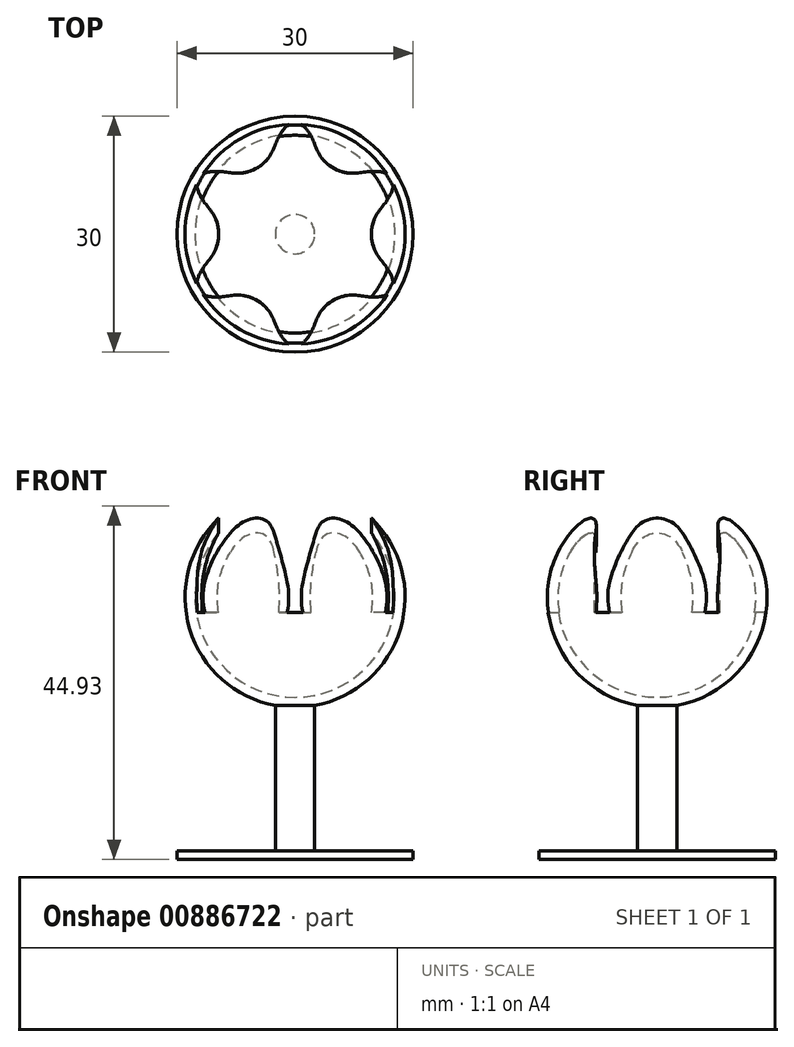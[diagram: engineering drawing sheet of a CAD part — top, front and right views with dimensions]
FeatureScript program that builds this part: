
annotation { "Feature Type Name" : "Feature", "Feature Type Description" : "" }
export const myFeature = defineFeature(function(context is Context, id is Id, definition is map)
    precondition{}
    {
        {
            var Q0;
            Q0=qCreatedBy(makeId("Top.planeOp"),FACE);
            var sketch = newSketch(context, id + "F0", { "sketchPlane" : qUnion([Q0])});
            skCircle(sketch, "E0", {"center": v(0, 0) * mm, "radius": 15 * mm});
            skSolve(sketch);
        }
        {
            var Q0;
            Q0 = qSketchRegion(id + "F0", true);
            extrude(context, id + "F1", {"entities" : qUnion([Q0]), "depth" : 1.1 * mm, "offsetDistance" : 25 * mm});
        }
        {
            var Q0;
            Q0=makeQuery(id+"F1.opExtrude","CAP_FACE",FACE,{"disambiguationData":[OSD([sQuery(id+"F0.wireOp",EDGE,"E0")])],"isStart":false});
            var sketch = newSketch(context, id + "F2", { "sketchPlane" : qUnion([Q0])});
            skCircle(sketch, "E1", {"center": v(0, 0) * mm, "radius": 2.5 * mm});
            skSolve(sketch);
        }
        {
            var Q0;
            Q0 = qSketchRegion(id + "F2", true);
            extrude(context, id + "F3", {"entities" : qUnion([Q0]), "operationType" : NewBodyOperationType.ADD, "depth" : 32.2 * mm, "offsetDistance" : 25 * mm});
        }
        {
            var Q0;
            Q0=makeQuery(id+"F3.opExtrude","CAP_FACE",FACE,{"disambiguationData":[OSD([sQuery(id+"F2.wireOp",EDGE,"E1")])],"isStart":false});
            var sketch = newSketch(context, id + "F4", { "sketchPlane" : qUnion([Q0])});
            skCircle(sketch, "E2", {"center": v(0, 0) * mm, "radius": 13.97 * mm});
            skPoint(sketch, "E3.orphan", {"position": v(0, 12.7) * mm});
            skLineSegment(sketch, "E4", {"start": v(0, 13.97) * mm, "end": v(0, -13.97) * mm});
            skSolve(sketch);
        }
        {
            var Q0;
            {var subQ0=sQuery(id+"F4.wireOp",EDGE,"E4");var subQ1=makeQuery(id+"F3.opExtrude","CAP_EDGE",EDGE,{"disambiguationData":[OSD([sQuery(id+"F2.wireOp",EDGE,"E1")])],"isStart":false});var subQ2=makeQuery(id+"F4.imprint","INTERSECT",VERTEX,{"disambiguationData":[OD(0.0)],"derivedFrom":[subQ1,subQ0]});Q0=makeQuery(id+"F4.imprint","IMPRINT",FACE,{"disambiguationData":[TD([[makeQuery(id+"F4.imprint","IMPRINT",EDGE,{"disambiguationData":[TD([[subQ2,-1.0]])],"derivedFrom":subQ0}),1.0]])]});}
            var sketch = newSketch(context, id + "F5", { "sketchPlane" : qUnion([Q0])});
            skCircle(sketch, "E5", {"center": v(0, 0) * mm, "radius": 12.7 * mm});
            skLineSegment(sketch, "E6", {"start": v(0, 12.7) * mm, "end": v(0, -12.7) * mm});
            skSolve(sketch);
        }
        {
            var Q0;
            {var subQ0=sQuery(id+"F4.wireOp",EDGE,"E4");var subQ1=sQuery(id+"F4.wireOp",EDGE,"E2");var subQ2=makeQuery(id+"F4.imprint","INTERSECT",VERTEX,{"disambiguationData":[OD(0.0)],"derivedFrom":[subQ1,subQ0]});Q0=makeQuery(id+"F4.imprint","IMPRINT",FACE,{"disambiguationData":[TD([[makeQuery(id+"F4.imprint","IMPRINT",EDGE,{"disambiguationData":[TD([[subQ2,-1.0]])],"derivedFrom":subQ1}),1.0]])]});}
            var Q1;
            Q1=sQuery(id+"F4.wireOp",EDGE,"E4");
            revolve(context, id + "F6", {"operationType" : NewBodyOperationType.ADD, "surfaceOperationType" : NewSurfaceOperationType.NEW, "entities" : qUnion([Q0]), "axis" : qUnion([Q1]), "revolveType" : RevolveType.FULL});
        }
        {
            var Q0;
            Q0=makeQuery(id+"F1.opExtrude","CAP_FACE",FACE,{"disambiguationData":[OSD([sQuery(id+"F0.wireOp",EDGE,"E0")])],"isStart":true});
            cPlane(context, id + "F7", {"entities" : qUnion([Q0]), "cplaneType" : CPlaneType.OFFSET, "offset" : 48.4 * mm, "oppositeDirection" : true, "width" : 150 * mm, "height" : 150 * mm});
        }
        {
            var Q0;
            Q0=qCreatedBy(id+"F7.planeOp",FACE);
            var sketch = newSketch(context, id + "F8", { "sketchPlane" : qUnion([Q0])});
            skCircle(sketch, "E7", {"center": v(0, 0) * mm, "radius": 14.16 * mm});
            skSolve(sketch);
        }
        {
            var Q0;
            Q0 = qSketchRegion(id + "F8", true);
            extrude(context, id + "F9", {"entities" : qUnion([Q0]), "operationType" : NewBodyOperationType.REMOVE, "depth" : 4.1 * mm, "offsetDistance" : 25 * mm});
        }
        {
            var Q0;
            Q0=makeQuery(id+"F9.boolean.opBoolean","COPY",FACE,{"derivedFrom":makeQuery(id+"F9.opExtrude","CAP_FACE",FACE,{"disambiguationData":[OSD([sQuery(id+"F8.wireOp",EDGE,"E7")])],"isStart":false})});
            var sketch = newSketch(context, id + "F10", { "sketchPlane" : qUnion([Q0])});
            skEllipse(sketch, "E8", {"center": v(0, 0) * mm, "majorRadius": 14.21 * mm, "minorRadius": 4.2 * mm, "majorAxis": v(0, -1)});
            skEllipse(sketch, "E9.1.0", {"center": v(0, 0) * mm, "majorRadius": 14.21 * mm, "minorRadius": 4.2 * mm, "majorAxis": v(0.87, 0.5)});
            skEllipse(sketch, "E9.2.0", {"center": v(0, 0) * mm, "majorRadius": 14.21 * mm, "minorRadius": 4.2 * mm, "majorAxis": v(-0.87, 0.5)});
            skSolve(sketch);
        }
        {
            var Q0;
            {var subQ0=sQuery(id+"F10.wireOp",EDGE,"E9.2.0");var subQ1=sQuery(id+"F10.wireOp",EDGE,"E8");var subQ2=makeQuery(id+"F10.imprint","INTERSECT",VERTEX,{"disambiguationData":[OD(0.0)],"derivedFrom":[subQ1,subQ0]});Q0=makeQuery(id+"F10.imprint","IMPRINT",FACE,{"disambiguationData":[TD([[makeQuery(id+"F10.imprint","IMPRINT",EDGE,{"disambiguationData":[TD([[subQ2,-1.0]])],"derivedFrom":subQ1}),1.0]])]});}
            var Q1;
            {var subQ0=sQuery(id+"F10.wireOp",EDGE,"E9.1.0");var subQ1=sQuery(id+"F10.wireOp",EDGE,"E8");var subQ2=makeQuery(id+"F10.imprint","INTERSECT",VERTEX,{"disambiguationData":[OD(0.0)],"derivedFrom":[subQ1,subQ0]});Q1=makeQuery(id+"F10.imprint","IMPRINT",FACE,{"disambiguationData":[TD([[makeQuery(id+"F10.imprint","IMPRINT",EDGE,{"disambiguationData":[TD([[subQ2,-1.0]])],"derivedFrom":subQ1}),-1.0]])]});}
            var Q2;
            {var subQ0=sQuery(id+"F10.wireOp",EDGE,"E9.1.0");var subQ1=sQuery(id+"F10.wireOp",EDGE,"E8");var subQ2=makeQuery(id+"F10.imprint","INTERSECT",VERTEX,{"disambiguationData":[OD(0.0)],"derivedFrom":[subQ1,subQ0]});Q2=makeQuery(id+"F10.imprint","IMPRINT",FACE,{"disambiguationData":[TD([[makeQuery(id+"F10.imprint","IMPRINT",EDGE,{"disambiguationData":[TD([[subQ2,-1.0]])],"derivedFrom":subQ1}),1.0]])]});}
            var Q3;
            {var subQ0=sQuery(id+"F10.wireOp",EDGE,"E9.2.0");var subQ1=sQuery(id+"F10.wireOp",EDGE,"E8");var subQ2=makeQuery(id+"F10.imprint","INTERSECT",VERTEX,{"disambiguationData":[OD(2.0)],"derivedFrom":[subQ1,subQ0]});Q3=makeQuery(id+"F10.imprint","IMPRINT",FACE,{"disambiguationData":[TD([[makeQuery(id+"F10.imprint","IMPRINT",EDGE,{"disambiguationData":[TD([[subQ2,-1.0]])],"derivedFrom":subQ1}),1.0]])]});}
            var Q4;
            {var subQ0=sQuery(id+"F10.wireOp",EDGE,"E9.2.0");var subQ1=sQuery(id+"F10.wireOp",EDGE,"E8");var subQ2=makeQuery(id+"F10.imprint","INTERSECT",VERTEX,{"disambiguationData":[OD(3.0)],"derivedFrom":[subQ1,subQ0]});Q4=makeQuery(id+"F10.imprint","IMPRINT",FACE,{"disambiguationData":[TD([[makeQuery(id+"F10.imprint","IMPRINT",EDGE,{"disambiguationData":[TD([[subQ2,-1.0]])],"derivedFrom":subQ1}),1.0]])]});}
            var Q5;
            {var subQ0=sQuery(id+"F10.wireOp",EDGE,"E9.2.0");var subQ1=sQuery(id+"F10.wireOp",EDGE,"E8");var subQ2=makeQuery(id+"F10.imprint","INTERSECT",VERTEX,{"disambiguationData":[OD(3.0)],"derivedFrom":[subQ1,subQ0]});Q5=makeQuery(id+"F10.imprint","IMPRINT",FACE,{"disambiguationData":[TD([[makeQuery(id+"F10.imprint","IMPRINT",EDGE,{"disambiguationData":[TD([[subQ2,-1.0]])],"derivedFrom":subQ1}),-1.0]])]});}
            var Q6;
            {var subQ0=sQuery(id+"F10.wireOp",EDGE,"E9.1.0");var subQ1=makeQuery(id+"F9.boolean.opBoolean","INTERSECT",EDGE,{"derivedFrom":[makeQuery(id+"F6.opRevolve","SWEPT_FACE",FACE,{"disambiguationData":[OSD([sQuery(id+"F4.wireOp",EDGE,"E2")])]}),makeQuery(id+"F9.opExtrude","CAP_FACE",FACE,{"disambiguationData":[OSD([sQuery(id+"F8.wireOp",EDGE,"E7")])],"isStart":false})]});var subQ2=makeQuery(id+"F10.imprint","INTERSECT",VERTEX,{"disambiguationData":[OD(1.0)],"derivedFrom":[subQ1,subQ0]});Q6=makeQuery(id+"F10.imprint","IMPRINT",FACE,{"disambiguationData":[TD([[makeQuery(id+"F10.imprint","IMPRINT",EDGE,{"disambiguationData":[TD([[subQ2,-1.0]])],"derivedFrom":subQ0}),1.0]])]});}
            var Q7;
            {var subQ0=sQuery(id+"F10.wireOp",EDGE,"E9.2.0");var subQ1=sQuery(id+"F10.wireOp",EDGE,"E8");var subQ2=makeQuery(id+"F10.imprint","INTERSECT",VERTEX,{"disambiguationData":[OD(2.0)],"derivedFrom":[subQ1,subQ0]});Q7=makeQuery(id+"F10.imprint","IMPRINT",FACE,{"disambiguationData":[TD([[makeQuery(id+"F10.imprint","IMPRINT",EDGE,{"disambiguationData":[TD([[subQ2,-1.0]])],"derivedFrom":subQ1}),-1.0]])]});}
            var Q8;
            {var subQ0=sQuery(id+"F10.wireOp",EDGE,"E9.2.0");var subQ1=makeQuery(id+"F9.boolean.opBoolean","INTERSECT",EDGE,{"derivedFrom":[makeQuery(id+"F6.opRevolve","SWEPT_FACE",FACE,{"disambiguationData":[OSD([sQuery(id+"F4.wireOp",EDGE,"E2")])]}),makeQuery(id+"F9.opExtrude","CAP_FACE",FACE,{"disambiguationData":[OSD([sQuery(id+"F8.wireOp",EDGE,"E7")])],"isStart":false})]});var subQ2=makeQuery(id+"F10.imprint","INTERSECT",VERTEX,{"disambiguationData":[OD(0.0)],"derivedFrom":[subQ1,subQ0]});Q8=makeQuery(id+"F10.imprint","IMPRINT",FACE,{"disambiguationData":[TD([[makeQuery(id+"F10.imprint","IMPRINT",EDGE,{"disambiguationData":[TD([[subQ2,1.0]])],"derivedFrom":subQ0}),1.0]])]});}
            var Q9;
            {var subQ0=sQuery(id+"F10.wireOp",EDGE,"E9.1.0");var subQ1=sQuery(id+"F10.wireOp",EDGE,"E8");var subQ2=makeQuery(id+"F10.imprint","INTERSECT",VERTEX,{"disambiguationData":[OD(2.0)],"derivedFrom":[subQ1,subQ0]});Q9=makeQuery(id+"F10.imprint","IMPRINT",FACE,{"disambiguationData":[TD([[makeQuery(id+"F10.imprint","IMPRINT",EDGE,{"disambiguationData":[TD([[subQ2,-1.0]])],"derivedFrom":subQ1}),-1.0]])]});}
            var Q10;
            {var subQ0=sQuery(id+"F10.wireOp",EDGE,"E8");var subQ1=makeQuery(id+"F9.boolean.opBoolean","INTERSECT",EDGE,{"derivedFrom":[makeQuery(id+"F6.opRevolve","SWEPT_FACE",FACE,{"disambiguationData":[OSD([sQuery(id+"F4.wireOp",EDGE,"E2")])]}),makeQuery(id+"F9.opExtrude","CAP_FACE",FACE,{"disambiguationData":[OSD([sQuery(id+"F8.wireOp",EDGE,"E7")])],"isStart":false})]});var subQ2=makeQuery(id+"F10.imprint","INTERSECT",VERTEX,{"disambiguationData":[OD(0.0)],"derivedFrom":[subQ1,subQ0]});Q10=makeQuery(id+"F10.imprint","IMPRINT",FACE,{"disambiguationData":[TD([[makeQuery(id+"F10.imprint","IMPRINT",EDGE,{"disambiguationData":[TD([[subQ2,1.0]])],"derivedFrom":subQ0}),1.0]])]});}
            var Q11;
            {var subQ1=sQuery(id+"F10.wireOp",EDGE,"E8");var subQ3=sQuery(id+"F10.wireOp",EDGE,"E9.1.0");var subQ5=makeQuery(id+"F10.imprint","INTERSECT",VERTEX,{"disambiguationData":[OD(3.0)],"derivedFrom":[subQ1,subQ3]});Q11=makeQuery(id+"F10.imprint","IMPRINT",FACE,{"disambiguationData":[TD([[makeQuery(id+"F10.imprint","IMPRINT",EDGE,{"disambiguationData":[TD([[subQ5,-1.0]])],"derivedFrom":subQ3}),-1.0]])]});}
            var Q12;
            {var subQ0=sQuery(id+"F10.wireOp",EDGE,"E9.2.0");var subQ1=makeQuery(id+"F9.boolean.opBoolean","INTERSECT",EDGE,{"derivedFrom":[makeQuery(id+"F6.opRevolve","SWEPT_FACE",FACE,{"disambiguationData":[OSD([sQuery(id+"F4.wireOp",EDGE,"E2")])]}),makeQuery(id+"F9.opExtrude","CAP_FACE",FACE,{"disambiguationData":[OSD([sQuery(id+"F8.wireOp",EDGE,"E7")])],"isStart":false})]});var subQ2=makeQuery(id+"F10.imprint","INTERSECT",VERTEX,{"disambiguationData":[OD(1.0)],"derivedFrom":[subQ1,subQ0]});Q12=makeQuery(id+"F10.imprint","IMPRINT",FACE,{"disambiguationData":[TD([[makeQuery(id+"F10.imprint","IMPRINT",EDGE,{"disambiguationData":[TD([[subQ2,-1.0]])],"derivedFrom":subQ0}),1.0]])]});}
            var Q13;
            {var subQ0=sQuery(id+"F10.wireOp",EDGE,"E9.2.0");var subQ5=sQuery(id+"F10.wireOp",EDGE,"E8");var subQ6=makeQuery(id+"F10.imprint","INTERSECT",VERTEX,{"disambiguationData":[OD(0.0)],"derivedFrom":[subQ5,subQ0]});Q13=makeQuery(id+"F10.imprint","IMPRINT",FACE,{"disambiguationData":[TD([[makeQuery(id+"F10.imprint","IMPRINT",EDGE,{"disambiguationData":[TD([[subQ6,-1.0]])],"derivedFrom":subQ5}),-1.0]])]});}
            var Q14;
            {var subQ0=sQuery(id+"F10.wireOp",EDGE,"E9.1.0");var subQ1=makeQuery(id+"F9.boolean.opBoolean","INTERSECT",EDGE,{"derivedFrom":[makeQuery(id+"F6.opRevolve","SWEPT_FACE",FACE,{"disambiguationData":[OSD([sQuery(id+"F4.wireOp",EDGE,"E2")])]}),makeQuery(id+"F9.opExtrude","CAP_FACE",FACE,{"disambiguationData":[OSD([sQuery(id+"F8.wireOp",EDGE,"E7")])],"isStart":false})]});var subQ2=makeQuery(id+"F10.imprint","INTERSECT",VERTEX,{"disambiguationData":[OD(0.0)],"derivedFrom":[subQ1,subQ0]});Q14=makeQuery(id+"F10.imprint","IMPRINT",FACE,{"disambiguationData":[TD([[makeQuery(id+"F10.imprint","IMPRINT",EDGE,{"disambiguationData":[TD([[subQ2,1.0]])],"derivedFrom":subQ0}),1.0]])]});}
            var Q15;
            {var subQ0=sQuery(id+"F10.wireOp",EDGE,"E9.2.0");var subQ1=sQuery(id+"F10.wireOp",EDGE,"E8");var subQ2=makeQuery(id+"F10.imprint","INTERSECT",VERTEX,{"disambiguationData":[OD(1.0)],"derivedFrom":[subQ1,subQ0]});Q15=makeQuery(id+"F10.imprint","IMPRINT",FACE,{"disambiguationData":[TD([[makeQuery(id+"F10.imprint","IMPRINT",EDGE,{"disambiguationData":[TD([[subQ2,-1.0]])],"derivedFrom":subQ1}),-1.0]])]});}
            var Q16;
            {var subQ0=sQuery(id+"F10.wireOp",EDGE,"E8");var subQ1=makeQuery(id+"F9.boolean.opBoolean","INTERSECT",EDGE,{"derivedFrom":[makeQuery(id+"F6.opRevolve","SWEPT_FACE",FACE,{"disambiguationData":[OSD([sQuery(id+"F4.wireOp",EDGE,"E2")])]}),makeQuery(id+"F9.opExtrude","CAP_FACE",FACE,{"disambiguationData":[OSD([sQuery(id+"F8.wireOp",EDGE,"E7")])],"isStart":false})]});var subQ2=makeQuery(id+"F10.imprint","INTERSECT",VERTEX,{"disambiguationData":[OD(1.0)],"derivedFrom":[subQ1,subQ0]});Q16=makeQuery(id+"F10.imprint","IMPRINT",FACE,{"disambiguationData":[TD([[makeQuery(id+"F10.imprint","IMPRINT",EDGE,{"disambiguationData":[TD([[subQ2,-1.0]])],"derivedFrom":subQ0}),1.0]])]});}
            var Q17;
            {var subQ1=sQuery(id+"F10.wireOp",EDGE,"E8");var subQ3=sQuery(id+"F10.wireOp",EDGE,"E9.1.0");var subQ5=makeQuery(id+"F10.imprint","INTERSECT",VERTEX,{"disambiguationData":[OD(1.0)],"derivedFrom":[subQ1,subQ3]});Q17=makeQuery(id+"F10.imprint","IMPRINT",FACE,{"disambiguationData":[TD([[makeQuery(id+"F10.imprint","IMPRINT",EDGE,{"disambiguationData":[TD([[subQ5,-1.0]])],"derivedFrom":subQ3}),-1.0]])]});}
            var Q18;
            {var subQ0=sQuery(id+"F10.wireOp",EDGE,"E9.2.0");var subQ1=sQuery(id+"F10.wireOp",EDGE,"E8");var subQ2=makeQuery(id+"F10.imprint","INTERSECT",VERTEX,{"disambiguationData":[OD(1.0)],"derivedFrom":[subQ1,subQ0]});Q18=makeQuery(id+"F10.imprint","IMPRINT",FACE,{"disambiguationData":[TD([[makeQuery(id+"F10.imprint","IMPRINT",EDGE,{"disambiguationData":[TD([[subQ2,-1.0]])],"derivedFrom":subQ1}),1.0]])]});}
            extrude(context, id + "F11", {"entities" : qUnion([Q0, Q1, Q2, Q3, Q4, Q5, Q6, Q7, Q8, Q9, Q10, Q11, Q12, Q13, Q14, Q15, Q16, Q17, Q18]), "operationType" : NewBodyOperationType.REMOVE, "oppositeDirection" : true, "depth" : 12.9 * mm, "offsetDistance" : 25 * mm});
        }
        {
            var Q0;
            {var subQ0=sQuery(id+"F5.wireOp",EDGE,"E6");var subQ1=sQuery(id+"F5.wireOp",EDGE,"E5");var subQ2=makeQuery(id+"F5.imprint","INTERSECT",VERTEX,{"disambiguationData":[OD(0.0)],"derivedFrom":[subQ1,subQ0]});Q0=makeQuery(id+"F5.imprint","IMPRINT",FACE,{"disambiguationData":[TD([[makeQuery(id+"F5.imprint","IMPRINT",EDGE,{"disambiguationData":[TD([[subQ2,-1.0]])],"derivedFrom":subQ1}),1.0]])]});}
            var Q1;
            Q1=sQuery(id+"F5.wireOp",EDGE,"E6");
            revolve(context, id + "F12", {"operationType" : NewBodyOperationType.REMOVE, "surfaceOperationType" : NewSurfaceOperationType.NEW, "entities" : qUnion([Q0]), "axis" : qUnion([Q1]), "revolveType" : RevolveType.FULL, "oppositeDirection" : true});
        }
        {
            var Q0;
            {var subQ0=sQuery(id+"F10.wireOp",EDGE,"E9.2.0");var subQ1=sQuery(id+"F10.wireOp",EDGE,"E8");Q0=makeQuery(id+"F11.boolean.opBoolean","COPY",EDGE,{"derivedFrom":makeQuery(id+"F11.opExtrude","SWEPT_EDGE",EDGE,{"disambiguationData":[OSD([subQ1,subQ0]),TDD([makeQuery(id+"F10.imprint","INTERSECT",VERTEX,{"disambiguationData":[OD(2.0)],"derivedFrom":[subQ1,subQ0]})])]})});}
            var Q1;
            {var subQ0=sQuery(id+"F10.wireOp",EDGE,"E9.1.0");var subQ1=sQuery(id+"F10.wireOp",EDGE,"E8");Q1=makeQuery(id+"F11.boolean.opBoolean","COPY",EDGE,{"derivedFrom":makeQuery(id+"F11.opExtrude","SWEPT_EDGE",EDGE,{"disambiguationData":[OSD([subQ1,subQ0]),TDD([makeQuery(id+"F10.imprint","INTERSECT",VERTEX,{"disambiguationData":[OD(1.0)],"derivedFrom":[subQ1,subQ0]})])]})});}
            var Q2;
            {var subQ0=sQuery(id+"F10.wireOp",EDGE,"E9.2.0");var subQ1=sQuery(id+"F10.wireOp",EDGE,"E9.1.0");Q2=makeQuery(id+"F11.boolean.opBoolean","COPY",EDGE,{"derivedFrom":makeQuery(id+"F11.opExtrude","SWEPT_EDGE",EDGE,{"disambiguationData":[OSD([subQ1,subQ0]),TDD([makeQuery(id+"F10.imprint","INTERSECT",VERTEX,{"disambiguationData":[OD(3.0)],"derivedFrom":[subQ1,subQ0]})])]})});}
            var Q3;
            {var subQ0=sQuery(id+"F10.wireOp",EDGE,"E9.2.0");var subQ1=sQuery(id+"F10.wireOp",EDGE,"E8");Q3=makeQuery(id+"F11.boolean.opBoolean","COPY",EDGE,{"derivedFrom":makeQuery(id+"F11.opExtrude","SWEPT_EDGE",EDGE,{"disambiguationData":[OSD([subQ1,subQ0]),TDD([makeQuery(id+"F10.imprint","INTERSECT",VERTEX,{"disambiguationData":[OD(0.0)],"derivedFrom":[subQ1,subQ0]})])]})});}
            var Q4;
            {var subQ0=sQuery(id+"F10.wireOp",EDGE,"E9.1.0");var subQ1=sQuery(id+"F10.wireOp",EDGE,"E8");Q4=makeQuery(id+"F11.boolean.opBoolean","COPY",EDGE,{"derivedFrom":makeQuery(id+"F11.opExtrude","SWEPT_EDGE",EDGE,{"disambiguationData":[OSD([subQ1,subQ0]),TDD([makeQuery(id+"F10.imprint","INTERSECT",VERTEX,{"disambiguationData":[OD(3.0)],"derivedFrom":[subQ1,subQ0]})])]})});}
            var Q5;
            {var subQ0=sQuery(id+"F10.wireOp",EDGE,"E9.2.0");var subQ1=sQuery(id+"F10.wireOp",EDGE,"E9.1.0");Q5=makeQuery(id+"F11.boolean.opBoolean","COPY",EDGE,{"derivedFrom":makeQuery(id+"F11.opExtrude","SWEPT_EDGE",EDGE,{"disambiguationData":[OSD([subQ1,subQ0]),TDD([makeQuery(id+"F10.imprint","INTERSECT",VERTEX,{"disambiguationData":[OD(1.0)],"derivedFrom":[subQ1,subQ0]})])]})});}
            fillet(context, id + "F13", {"entities" : qUnion([Q0, Q1, Q2, Q3, Q4, Q5]), "radius" : 5 * mm, "tangentPropagation" : true, "allowEdgeOverflow" : false});
        }
    });
